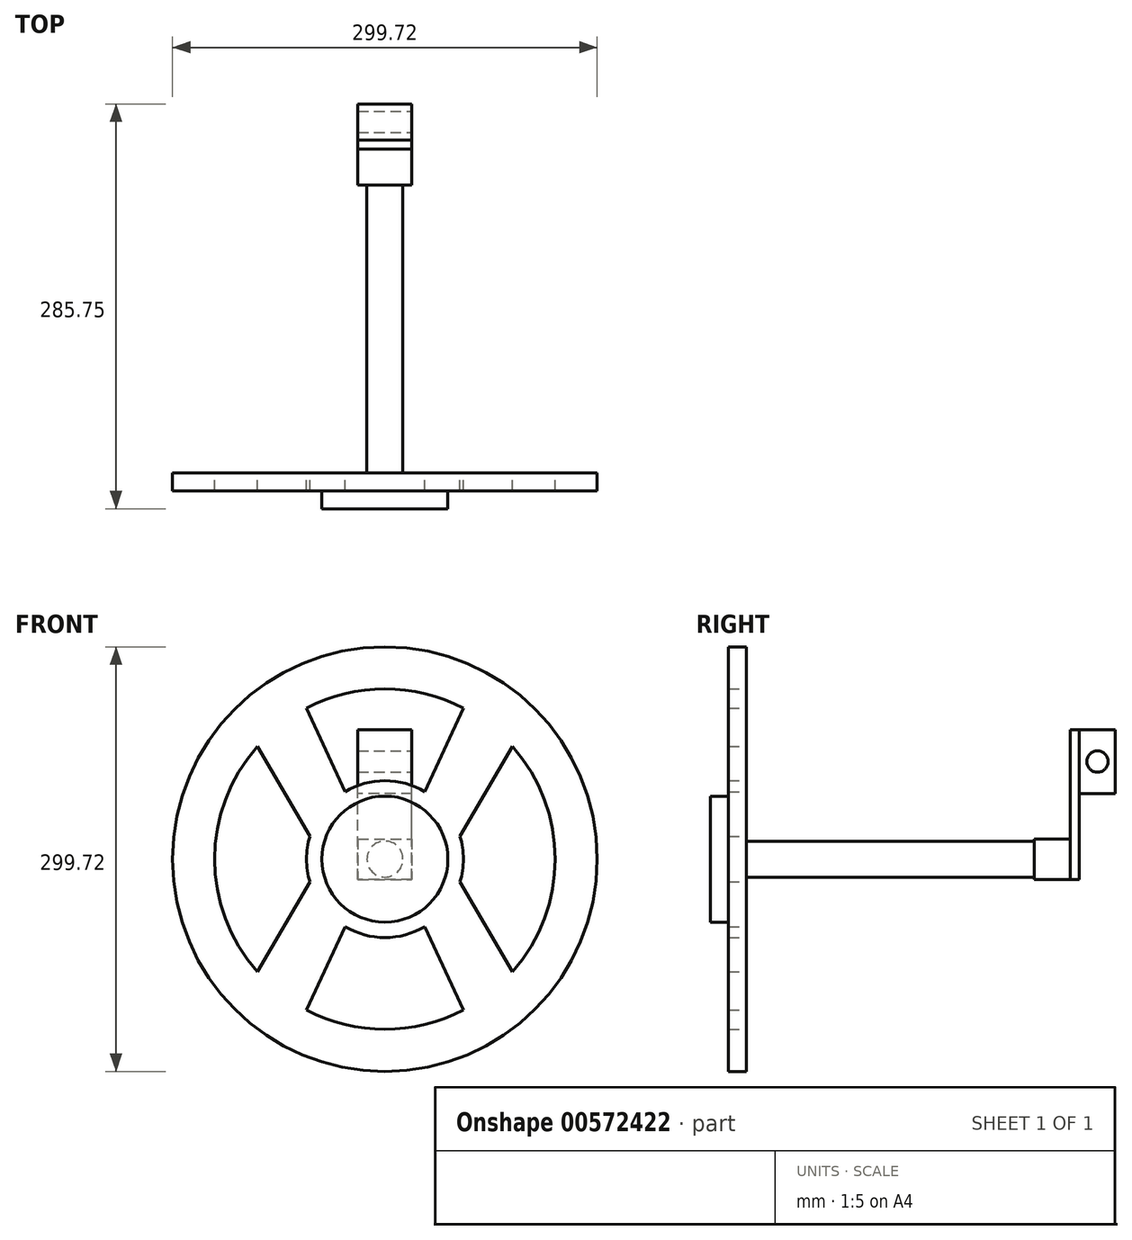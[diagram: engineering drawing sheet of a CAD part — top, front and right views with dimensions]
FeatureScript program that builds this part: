
annotation { "Feature Type Name" : "Feature", "Feature Type Description" : "" }
export const myFeature = defineFeature(function(context is Context, id is Id, definition is map)
    precondition{}
    {
        {
            var Q0;
            Q0=qCreatedBy(makeId("Front.planeOp"),FACE);
            var sketch = newSketch(context, id + "F0", { "sketchPlane" : qUnion([Q0])});
            skCircle(sketch, "E0", {"center": v(0, 0) * mm, "radius": 149.86 * mm});
            skCircle(sketch, "E1", {"center": v(0, 0) * mm, "radius": 120.17 * mm});
            skCircle(sketch, "E2", {"center": v(0, 0) * mm, "radius": 55.37 * mm});
            skCircle(sketch, "E3", {"center": v(0, 0) * mm, "radius": 26.65 * mm});
            skLineSegment(sketch, "E4.MirrorCS", {"start": v(52.96, -16.14) * mm, "end": v(90.07, -79.56) * mm});
            skLineSegment(sketch, "E5.MirrorCS", {"start": v(52.96, 16.14) * mm, "end": v(90.07, 79.56) * mm});
            skLineSegment(sketch, "E6.MirrorCS", {"start": v(-52.96, -16.14) * mm, "end": v(-90.07, -79.56) * mm});
            skLineSegment(sketch, "E7.MirrorCS", {"start": v(-52.96, 16.14) * mm, "end": v(-90.07, 79.56) * mm});
            skLineSegment(sketch, "E8", {"start": v(-55.5, 106.6) * mm, "end": v(-28.25, 47.62) * mm});
            skLineSegment(sketch, "E9.MirrorCS", {"start": v(-55.5, -106.6) * mm, "end": v(-28.25, -47.62) * mm});
            skLineSegment(sketch, "E10.MirrorCS", {"start": v(55.5, -106.6) * mm, "end": v(28.25, -47.62) * mm});
            skLineSegment(sketch, "E11.MirrorCS", {"start": v(55.5, 106.6) * mm, "end": v(28.25, 47.62) * mm});
            skSolve(sketch);
        }
        {
            var Q0;
            Q0=makeQuery(id+"F0.imprint","IMPRINT",FACE,{"disambiguationData":[TD([[makeQuery(id+"F0.imprint","IMPRINT",EDGE,{"derivedFrom":sQuery(id+"F0.wireOp",EDGE,"E3")}),-1.0]])]});
            var Q1;
            {var subQ0=sQuery(id+"F0.wireOp",EDGE,"E7.MirrorCS");Q1=makeQuery(id+"F0.imprint","IMPRINT",FACE,{"disambiguationData":[TD([[makeQuery(id+"F0.imprint","IMPRINT",EDGE,{"derivedFrom":subQ0}),-1.0]])]});}
            var Q2;
            Q2=makeQuery(id+"F0.imprint","IMPRINT",FACE,{"disambiguationData":[TD([[makeQuery(id+"F0.imprint","IMPRINT",EDGE,{"derivedFrom":sQuery(id+"F0.wireOp",EDGE,"E0")}),1.0]])]});
            var Q3;
            {var subQ0=sQuery(id+"F0.wireOp",EDGE,"E6.MirrorCS");Q3=makeQuery(id+"F0.imprint","IMPRINT",FACE,{"disambiguationData":[TD([[makeQuery(id+"F0.imprint","IMPRINT",EDGE,{"derivedFrom":subQ0}),1.0]])]});}
            var Q4;
            {var subQ0=sQuery(id+"F0.wireOp",EDGE,"E4.MirrorCS");Q4=makeQuery(id+"F0.imprint","IMPRINT",FACE,{"disambiguationData":[TD([[makeQuery(id+"F0.imprint","IMPRINT",EDGE,{"derivedFrom":subQ0}),-1.0]])]});}
            var Q5;
            {var subQ0=sQuery(id+"F0.wireOp",EDGE,"E5.MirrorCS");Q5=makeQuery(id+"F0.imprint","IMPRINT",FACE,{"disambiguationData":[TD([[makeQuery(id+"F0.imprint","IMPRINT",EDGE,{"derivedFrom":subQ0}),1.0]])]});}
            extrude(context, id + "F1", {"entities" : qUnion([Q0, Q1, Q2, Q3, Q4, Q5]), "depth" : 12.7 * mm, "offsetDistance" : 25.4 * mm});
        }
        {
            var Q0;
            Q0=qCreatedBy(makeId("Front.planeOp"),FACE);
            var sketch = newSketch(context, id + "F2", { "sketchPlane" : qUnion([Q0])});
            skCircle(sketch, "E12", {"center": v(0, 0) * mm, "radius": 44.45 * mm});
            skSolve(sketch);
        }
        {
            var Q0;
            Q0 = qSketchRegion(id + "F2", true);
            extrude(context, id + "F3", {"entities" : qUnion([Q0]), "operationType" : NewBodyOperationType.ADD, "depth" : 25.4 * mm, "offsetDistance" : 25.4 * mm});
        }
        {
            var Q0;
            Q0=qCreatedBy(makeId("Front.planeOp"),FACE);
            var sketch = newSketch(context, id + "F4", { "sketchPlane" : qUnion([Q0])});
            skCircle(sketch, "E13", {"center": v(0, 0) * mm, "radius": 12.7 * mm});
            skSolve(sketch);
        }
        {
            var Q0;
            Q0=makeQuery(id+"F4.imprint","IMPRINT",FACE,{"disambiguationData":[TD([[makeQuery(id+"F4.imprint","IMPRINT",EDGE,{"derivedFrom":sQuery(id+"F4.wireOp",EDGE,"E13")}),1.0]])]});
            extrude(context, id + "F5", {"entities" : qUnion([Q0]), "operationType" : NewBodyOperationType.ADD, "oppositeDirection" : true, "depth" : 203.2 * mm, "offsetDistance" : 25.4 * mm});
        }
        {
            var Q0;
            Q0=makeQuery(id+"F5.opExtrude","CAP_FACE",FACE,{"disambiguationData":[OSD([sQuery(id+"F4.wireOp",EDGE,"E13")])],"isStart":false});
            var sketch = newSketch(context, id + "F6", { "sketchPlane" : qUnion([Q0])});
            skLineSegment(sketch, "E14.bottom", {"start": v(19.05, 14.3) * mm, "end": v(-19.05, 14.3) * mm});
            skLineSegment(sketch, "E14.top", {"start": v(19.05, -14.3) * mm, "end": v(-19.05, -14.3) * mm});
            skLineSegment(sketch, "E14.left", {"start": v(19.05, 14.3) * mm, "end": v(19.05, -14.3) * mm});
            skLineSegment(sketch, "E14.right", {"start": v(-19.05, 14.3) * mm, "end": v(-19.05, -14.3) * mm});
            skPoint(sketch, "E14.middle", {"position": v(0, 0) * mm});
            skSolve(sketch);
        }
        {
            var Q0;
            Q0=makeQuery(id+"F6.imprint","IMPRINT",FACE,{"disambiguationData":[TD([[makeQuery(id+"F6.imprint","IMPRINT",EDGE,{"derivedFrom":sQuery(id+"F6.wireOp",EDGE,"E14.bottom")}),1.0]])]});
            var Q1;
            Q1=makeQuery(id+"F6.imprint","IMPRINT",FACE,{"disambiguationData":[TD([[makeQuery(id+"F6.imprint","IMPRINT",EDGE,{"derivedFrom":makeQuery(id+"F5.opExtrude","CAP_EDGE",EDGE,{"disambiguationData":[OSD([sQuery(id+"F4.wireOp",EDGE,"E13")])],"isStart":false})}),-1.0]])]});
            extrude(context, id + "F7", {"entities" : qUnion([Q0, Q1]), "operationType" : NewBodyOperationType.ADD, "depth" : 25.4 * mm, "offsetDistance" : 25.4 * mm});
        }
        {
            var Q0;
            Q0=makeQuery(id+"F7.opExtrude","CAP_FACE",FACE,{"disambiguationData":[OSD([sQuery(id+"F6.wireOp",EDGE,"E14.bottom"),sQuery(id+"F6.wireOp",EDGE,"E14.top"),sQuery(id+"F6.wireOp",EDGE,"E14.left"),sQuery(id+"F6.wireOp",EDGE,"E14.right")])],"isStart":false});
            var sketch = newSketch(context, id + "F8", { "sketchPlane" : qUnion([Q0])});
            skLineSegment(sketch, "E15", {"start": v(-18.95, 0) * mm, "end": v(-18.95, -14.3) * mm, "construction": true});
            skLineSegment(sketch, "E16", {"start": v(6.11, 0) * mm, "end": v(6.11, -14.3) * mm, "construction": true});
            skLineSegment(sketch, "E17.bottom", {"start": v(-18.95, -14.3) * mm, "end": v(19.15, -14.3) * mm});
            skLineSegment(sketch, "E17.top", {"start": v(-18.95, 91.4) * mm, "end": v(19.15, 91.4) * mm});
            skLineSegment(sketch, "E17.left", {"start": v(-18.95, -14.3) * mm, "end": v(-18.95, 91.4) * mm});
            skLineSegment(sketch, "E17.right", {"start": v(19.15, -14.3) * mm, "end": v(19.15, 91.4) * mm});
            skSolve(sketch);
        }
        {
            var Q0;
            {var subQ0=sQuery(id+"F8.wireOp",EDGE,"E17.top");Q0=makeQuery(id+"F8.imprint","IMPRINT",FACE,{"disambiguationData":[TD([[makeQuery(id+"F8.imprint","IMPRINT",EDGE,{"derivedFrom":subQ0}),-1.0]])]});}
            var Q1;
            {var subQ0=sQuery(id+"F8.wireOp",EDGE,"E17.bottom");Q1=makeQuery(id+"F8.imprint","IMPRINT",FACE,{"disambiguationData":[TD([[makeQuery(id+"F8.imprint","IMPRINT",EDGE,{"derivedFrom":subQ0}),-1.0]])]});}
            extrude(context, id + "F9", {"entities" : qUnion([Q0, Q1]), "operationType" : NewBodyOperationType.ADD, "depth" : 6.35 * mm, "offsetDistance" : 25.4 * mm});
        }
        {
            var Q0;
            Q0=makeQuery(id+"F9.opExtrude","CAP_FACE",FACE,{"disambiguationData":[OSD([sQuery(id+"F8.wireOp",EDGE,"E17.bottom"),sQuery(id+"F8.wireOp",EDGE,"E17.top"),sQuery(id+"F8.wireOp",EDGE,"E17.left"),sQuery(id+"F8.wireOp",EDGE,"E17.right")])],"isStart":false});
            var sketch = newSketch(context, id + "F10", { "sketchPlane" : qUnion([Q0])});
            skLineSegment(sketch, "E18", {"start": v(-18.95, 46.36) * mm, "end": v(19.15, 46.36) * mm});
            skSolve(sketch);
        }
        {
            var Q0;
            {var subQ0=sQuery(id+"F10.wireOp",EDGE,"E18");Q0=makeQuery(id+"F10.imprint","IMPRINT",FACE,{"disambiguationData":[TD([[makeQuery(id+"F10.imprint","IMPRINT",EDGE,{"derivedFrom":subQ0}),1.0]])]});}
            extrude(context, id + "F11", {"entities" : qUnion([Q0]), "depth" : 25.4 * mm, "offsetDistance" : 25.4 * mm});
        }
        {
            var Q0;
            Q0=makeQuery(id+"F11.opExtrude","SWEPT_FACE",FACE,{"disambiguationData":[OSD([sQuery(id+"F8.wireOp",EDGE,"E17.left")])]});
            var sketch = newSketch(context, id + "F12", { "sketchPlane" : qUnion([Q0])});
            skLineSegment(sketch, "E19", {"start": v(247.65, 91.4) * mm, "end": v(247.65, 46.36) * mm, "construction": true});
            skLineSegment(sketch, "E20", {"start": v(234.95, 68.88) * mm, "end": v(260.35, 68.88) * mm, "construction": true});
            skCircle(sketch, "E21", {"center": v(247.65, 68.88) * mm, "radius": 7.54 * mm});
            skSolve(sketch);
        }
        {
            var Q0;
            Q0=makeQuery(id+"F12.imprint","IMPRINT",FACE,{"disambiguationData":[TD([[makeQuery(id+"F12.imprint","IMPRINT",EDGE,{"derivedFrom":sQuery(id+"F12.wireOp",EDGE,"E21")}),1.0]])]});
            extrude(context, id + "F13", {"entities" : qUnion([Q0]), "operationType" : NewBodyOperationType.REMOVE, "oppositeDirection" : true, "depth" : 44.2 * mm, "offsetDistance" : 25.4 * mm});
        }
    });
